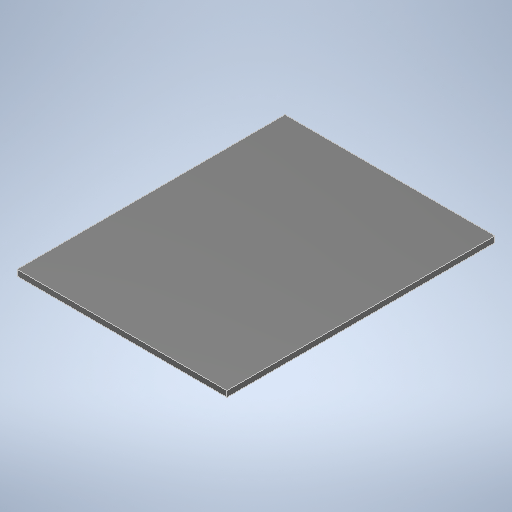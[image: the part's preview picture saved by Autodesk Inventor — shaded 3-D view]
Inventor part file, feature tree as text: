
AUTODESK INVENTOR PART (.ipt)
format: ipt  version: 2025 (Build 290162000, 162)  size: 241,152 bytes
history: native  units: mm
features: extrude x1, sketch x1
ambient origin geometry x8: Origin, YZ Plane, XZ Plane, XY Plane, X Axis, Y Axis, Z Axis, Center Point
bodies: Solid1 (feature_tree)
feature tree (2):
  extrude  "Extrusion1"  Depth=456.0mm
  sketch  "Sketch1"  dims[d0=582.0mm d1=456.0mm d2=12.7mm d3=0.0mm]
